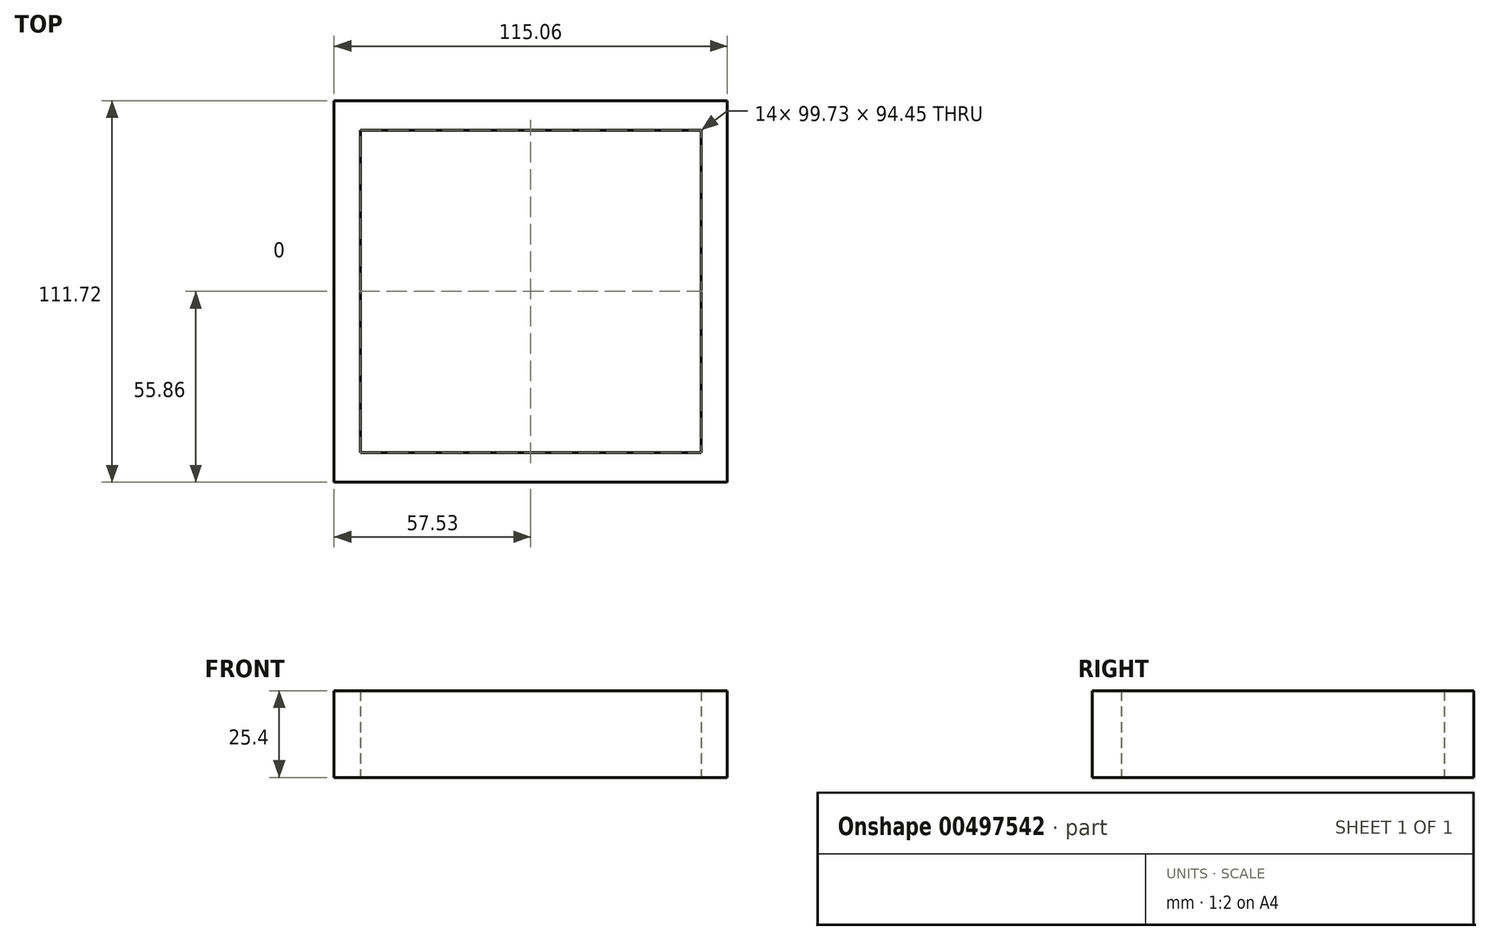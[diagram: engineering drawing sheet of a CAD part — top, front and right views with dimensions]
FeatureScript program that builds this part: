
annotation { "Feature Type Name" : "Feature", "Feature Type Description" : "" }
export const myFeature = defineFeature(function(context is Context, id is Id, definition is map)
    precondition{}
    {
        {
            var Q0;
            Q0=qCreatedBy(makeId("Top.planeOp"),FACE);
            var sketch = newSketch(context, id + "F0", { "sketchPlane" : qUnion([Q0])});
            skLineSegment(sketch, "E0.bottom", {"start": v(-57.53, 55.86) * mm, "end": v(57.53, 55.86) * mm});
            skLineSegment(sketch, "E0.top", {"start": v(-57.53, -55.86) * mm, "end": v(57.53, -55.86) * mm});
            skLineSegment(sketch, "E0.left", {"start": v(-57.53, 55.86) * mm, "end": v(-57.53, -55.86) * mm});
            skLineSegment(sketch, "E0.right", {"start": v(57.53, 55.86) * mm, "end": v(57.53, -55.86) * mm});
            skPoint(sketch, "E0.middle", {"position": v(0, 0) * mm});
            skLineSegment(sketch, "E1.bottom", {"start": v(-43.63, 41) * mm, "end": v(43.63, 41) * mm});
            skLineSegment(sketch, "E1.top", {"start": v(-43.63, -41) * mm, "end": v(43.63, -41) * mm});
            skLineSegment(sketch, "E1.left", {"start": v(-43.63, 41) * mm, "end": v(-43.63, -41) * mm});
            skLineSegment(sketch, "E1.right", {"start": v(43.63, 41) * mm, "end": v(43.63, -41) * mm});
            skLineSegment(sketch, "E2.bottom", {"start": v(-49.86, 47.23) * mm, "end": v(49.86, 47.23) * mm});
            skLineSegment(sketch, "E2.top", {"start": v(-49.86, -47.23) * mm, "end": v(49.86, -47.23) * mm});
            skLineSegment(sketch, "E2.left", {"start": v(-49.86, 47.23) * mm, "end": v(-49.86, -47.23) * mm});
            skLineSegment(sketch, "E2.right", {"start": v(49.86, 47.23) * mm, "end": v(49.86, -47.23) * mm});
            skSolve(sketch);
        }
        {
            var Q0;
            Q0=makeQuery(id+"F0.imprint","IMPRINT",FACE,{"disambiguationData":[TD([[makeQuery(id+"F0.imprint","IMPRINT",EDGE,{"derivedFrom":sQuery(id+"F0.wireOp",EDGE,"E0.bottom")}),-1.0]])]});
            extrude(context, id + "F1", {"entities" : qUnion([Q0]), "depth" : 25.4 * mm});
        }
    });
